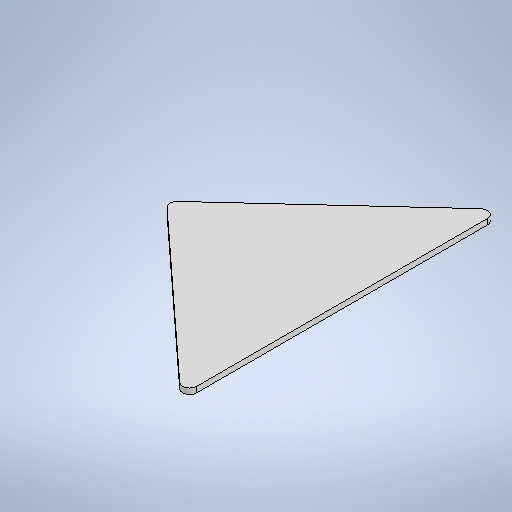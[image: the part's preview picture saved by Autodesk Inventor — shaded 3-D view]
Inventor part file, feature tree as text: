
AUTODESK INVENTOR PART (.ipt)
format: ipt  version: 2025.1 (Build 291241020, 241B)  size: 264,704 bytes
history: native  units: mm
features: other x2, sheet_metal_op x1, chamfer x1, sketch x1
ambient origin geometry x8: Origin, YZ Plane, XZ Plane, XY Plane, X Axis, Y Axis, Z Axis, Center Point
bodies: Solid1 (feature_tree)
feature tree (5):
  sheet_metal_op  "Face1"
  chamfer  "Corner Round2"
  sketch  "Sketch1"  dims[d1=46.0mm d2=0.8mm d6=1.0mm d9=25.0mm]
  other  "Plate1"
  other  "Definition1"
